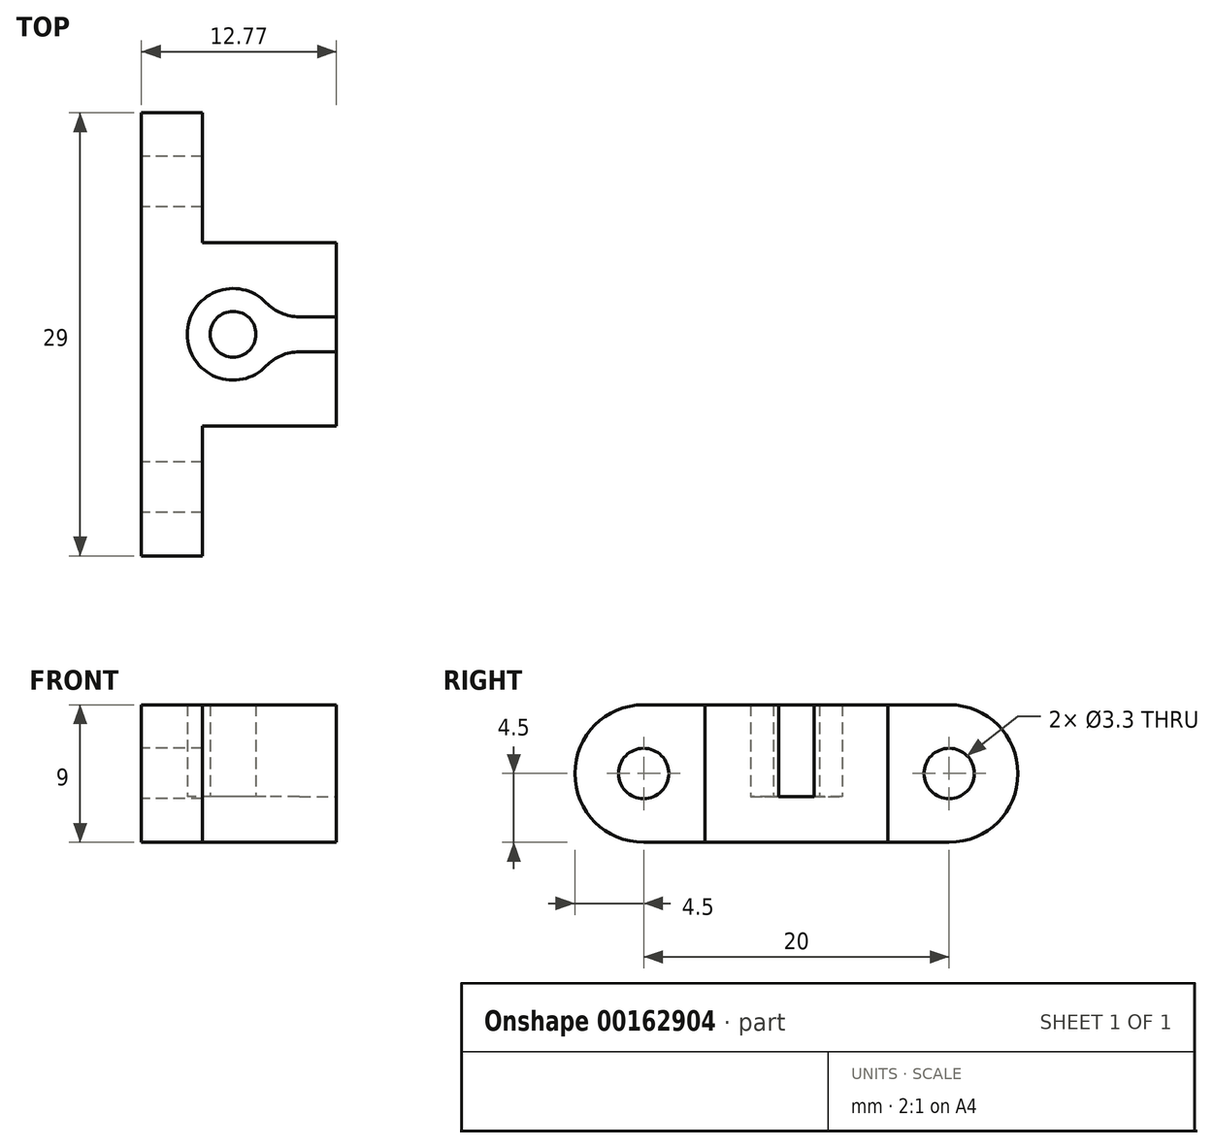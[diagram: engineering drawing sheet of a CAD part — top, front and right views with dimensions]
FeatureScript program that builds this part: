
annotation { "Feature Type Name" : "Feature", "Feature Type Description" : "" }
export const myFeature = defineFeature(function(context is Context, id is Id, definition is map)
    precondition{}
    {
        {
            var Q0;
            Q0=qCreatedBy(makeId("Top.planeOp"),FACE);
            var sketch = newSketch(context, id + "F0", { "sketchPlane" : qUnion([Q0])});
            skLineSegment(sketch, "E0", {"start": v(2.77, 1.15) * mm, "end": v(6.77, 1.15) * mm});
            skLineSegment(sketch, "E1.MirrorCS", {"start": v(2.77, -1.15) * mm, "end": v(6.77, -1.15) * mm});
            skArc(sketch, "E2", {"start": v(2.77, 1.15) * mm, "mid": v(-3, 0) * mm, "end": v(2.77, -1.15) * mm});
            skCircle(sketch, "E3", {"center": v(0, 0) * mm, "radius": 1.5 * mm});
            skLineSegment(sketch, "E4", {"start": v(6.77, 1.15) * mm, "end": v(6.77, 6) * mm});
            skLineSegment(sketch, "E5", {"start": v(6.77, 6) * mm, "end": v(-6, 6) * mm});
            skLineSegment(sketch, "E6", {"start": v(-6, 6) * mm, "end": v(-6, 0) * mm});
            skLineSegment(sketch, "E7.MirrorCS", {"start": v(-6, -6) * mm, "end": v(-6, 0) * mm});
            skLineSegment(sketch, "E8.MirrorCS", {"start": v(6.77, -6) * mm, "end": v(-6, -6) * mm});
            skLineSegment(sketch, "E9.MirrorCS", {"start": v(6.77, -1.15) * mm, "end": v(6.77, -6) * mm});
            skSolve(sketch);
        }
        {
            var Q0;
            Q0=makeQuery(id+"F0.imprint","IMPRINT",FACE,{"disambiguationData":[TD([[makeQuery(id+"F0.imprint","IMPRINT",EDGE,{"derivedFrom":sQuery(id+"F0.wireOp",EDGE,"E0")}),1.0]])]});
            var Q1;
            Q1=makeQuery(id+"F0.imprint","IMPRINT",FACE,{"disambiguationData":[TD([[makeQuery(id+"F0.imprint","IMPRINT",EDGE,{"derivedFrom":sQuery(id+"F0.wireOp",EDGE,"E3")}),1.0]])]});
            extrude(context, id + "F1", {"entities" : qUnion([Q0, Q1]), "depth" : 6 * mm});
        }
        {
            var Q0;
            Q0=makeQuery(id+"F1.opExtrude","CAP_FACE",FACE,{"disambiguationData":[OSD([sQuery(id+"F0.wireOp",EDGE,"E0"),sQuery(id+"F0.wireOp",EDGE,"E1.MirrorCS"),sQuery(id+"F0.wireOp",EDGE,"E2"),sQuery(id+"F0.wireOp",EDGE,"E4"),sQuery(id+"F0.wireOp",EDGE,"E5"),sQuery(id+"F0.wireOp",EDGE,"E6"),sQuery(id+"F0.wireOp",EDGE,"E7.MirrorCS"),sQuery(id+"F0.wireOp",EDGE,"E8.MirrorCS"),sQuery(id+"F0.wireOp",EDGE,"E9.MirrorCS")])],"isStart":true});
            var sketch = newSketch(context, id + "F2", { "sketchPlane" : qUnion([Q0])});
            skLineSegment(sketch, "E10.bottom", {"start": v(-6, 6) * mm, "end": v(6.77, 6) * mm});
            skLineSegment(sketch, "E10.top", {"start": v(-6, -6) * mm, "end": v(6.77, -6) * mm});
            skLineSegment(sketch, "E10.left", {"start": v(-6, 6) * mm, "end": v(-6, -6) * mm});
            skLineSegment(sketch, "E10.right", {"start": v(6.77, 6) * mm, "end": v(6.77, -6) * mm});
            skSolve(sketch);
        }
        {
            var Q0;
            Q0 = qSketchRegion(id + "F2", true);
            extrude(context, id + "F3", {"entities" : qUnion([Q0]), "operationType" : NewBodyOperationType.ADD, "depth" : 3 * mm});
        }
        {
            var Q0;
            Q0=makeQuery(id+"F1.opExtrude","SWEPT_EDGE",EDGE,{"disambiguationData":[OSD([sQuery(id+"F0.wireOp",EDGE,"E1.MirrorCS"),sQuery(id+"F0.wireOp",EDGE,"E2")])]});
            var Q1;
            Q1=makeQuery(id+"F1.opExtrude","SWEPT_EDGE",EDGE,{"disambiguationData":[OSD([sQuery(id+"F0.wireOp",EDGE,"E0"),sQuery(id+"F0.wireOp",EDGE,"E2")])]});
            fillet(context, id + "F4", {"entities" : qUnion([Q0, Q1]), "radius" : 3 * mm, "tangentPropagation" : true, "allowEdgeOverflow" : false});
        }
        {
            var Q0;
            Q0=makeQuery(id+"F3.boolean.opBoolean","MERGE",FACE,{"derivedFrom":[makeQuery(id+"F1.opExtrude","SWEPT_FACE",FACE,{"disambiguationData":[OSD([sQuery(id+"F0.wireOp",EDGE,"E6"),sQuery(id+"F0.wireOp",EDGE,"E7.MirrorCS")])]}),makeQuery(id+"F3.opExtrude","SWEPT_FACE",FACE,{"disambiguationData":[OSD([sQuery(id+"F2.wireOp",EDGE,"E10.left")])]})]});
            var sketch = newSketch(context, id + "F5", { "sketchPlane" : qUnion([Q0])});
            skLineSegment(sketch, "E11", {"start": v(0, 6) * mm, "end": v(-10, 6) * mm});
            skArc(sketch, "E12", {"start": v(-10, 6) * mm, "mid": v(-13.18, 4.68) * mm, "end": v(-14.5, 1.5) * mm});
            skPoint(sketch, "E12.centerSnap0", {"position": v(-6, 1.5) * mm});
            skLineSegment(sketch, "E13", {"start": v(-6, 1.5) * mm, "end": v(0, 1.5) * mm, "construction": true});
            skLineSegment(sketch, "E14.MirrorCS", {"start": v(0, -3) * mm, "end": v(-10, -3) * mm});
            skArc(sketch, "E15.MirrorCS", {"start": v(-10, -3) * mm, "mid": v(-13.18, -1.68) * mm, "end": v(-14.5, 1.5) * mm});
            skArc(sketch, "E16.MirrorCS", {"start": v(10, -3) * mm, "mid": v(13.18, -1.68) * mm, "end": v(14.5, 1.5) * mm});
            skLineSegment(sketch, "E17.MirrorCS", {"start": v(6, 1.5) * mm, "end": v(0, 1.5) * mm, "construction": true});
            skLineSegment(sketch, "E18.MirrorCS", {"start": v(0, -3) * mm, "end": v(10, -3) * mm});
            skLineSegment(sketch, "E19.MirrorCS", {"start": v(0, 6) * mm, "end": v(10, 6) * mm});
            skPoint(sketch, "E20.MirrorP", {"position": v(6, 1.5) * mm});
            skArc(sketch, "E21.MirrorCS", {"start": v(10, 6) * mm, "mid": v(13.18, 4.68) * mm, "end": v(14.5, 1.5) * mm});
            skSolve(sketch);
        }
        {
            var Q0;
            {var subQ3=sQuery(id+"F5.wireOp",EDGE,"E12");Q0=makeQuery(id+"F5.imprint","IMPRINT",FACE,{"disambiguationData":[TD([[makeQuery(id+"F5.imprint","IMPRINT",EDGE,{"derivedFrom":subQ3}),1.0]])]});}
            var Q1;
            {var subQ4=sQuery(id+"F5.wireOp",EDGE,"E16.MirrorCS");Q1=makeQuery(id+"F5.imprint","IMPRINT",FACE,{"disambiguationData":[TD([[makeQuery(id+"F5.imprint","IMPRINT",EDGE,{"derivedFrom":subQ4}),1.0]])]});}
            extrude(context, id + "F6", {"entities" : qUnion([Q0, Q1]), "operationType" : NewBodyOperationType.ADD, "oppositeDirection" : true, "depth" : 4 * mm});
        }
        {
            var Q0;
            Q0=sQuery(id+"F5.wireOp",VERTEX,"E12.center");
            var Q1;
            Q1=sQuery(id+"F5.wireOp",VERTEX,"E16.MirrorCS.center");
            var Q2;
            Q2=makeQuery(id+"F1.opExtrude","SWEPT_BODY",BODY,{"disambiguationData":[OSD([sQuery(id+"F0.wireOp",EDGE,"E0"),sQuery(id+"F0.wireOp",EDGE,"E1.MirrorCS"),sQuery(id+"F0.wireOp",EDGE,"E2"),sQuery(id+"F0.wireOp",EDGE,"E4"),sQuery(id+"F0.wireOp",EDGE,"E5"),sQuery(id+"F0.wireOp",EDGE,"E6"),sQuery(id+"F0.wireOp",EDGE,"E7.MirrorCS"),sQuery(id+"F0.wireOp",EDGE,"E8.MirrorCS"),sQuery(id+"F0.wireOp",EDGE,"E9.MirrorCS")])]});
            hole(context, id + "F7", {"style" : HoleStyle.SIMPLE, "endStyle" : HoleEndStyle.THROUGH, "standardTappedOrClearance" : lookupTablePath({ "standard" : "ISO", "fit" : "Normal", "size" : "M3", "type" : "Clearance" }), "standardBlindInLast" : lookupTablePath({ "fit" : "Standard", "standard" : "ISO", "size" : "M3", "type" : "Clearance" }), "holeDiameter" : 3.3 * mm, "isTappedThrough" : true, "tappedDepth" : 12 * mm, "tapClearance" : 3, "startFromSketch" : true, "locations" : qUnion([Q0, Q1]), "scope" : qUnion([Q2])});
        }
    });
